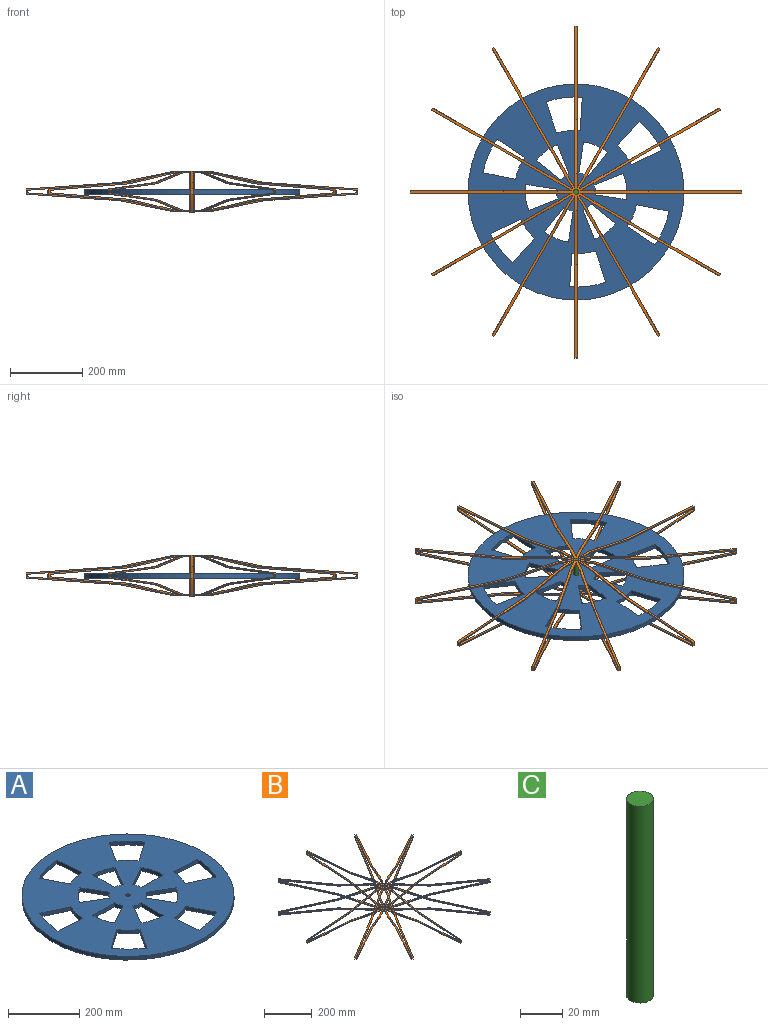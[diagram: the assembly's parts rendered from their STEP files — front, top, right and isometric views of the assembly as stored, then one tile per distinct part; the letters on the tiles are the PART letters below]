
ASSEMBLY  parts=3 mates=2
PART A: 52 faces, bbox 596.9x596.9x12.7 mm
  f0: plane 596.9x596.9mm, normal (0,0,-1), area 207289.9mm2, adj f2,f3,f4,f5,f6,f7,f8,f9
  f1: plane 596.9x596.9mm, normal (0,0,1), area 207289.9mm2, adj f2,f3,f4,f5,f6,f7,f8,f9
  f2: cylinder r=298.45mm len=596.9mm, axis (0,0,-1), area 23815.3mm2, adj f0,f1
  f3: cylinder r=6.35mm len=12.7mm, axis (0,0,-1), area 506.7mm2, adj f0,f1
  f4: plane 75.03x43.12mm, normal (0.5,-0.87,0), area 1099.1mm2, adj f0,f1,f5,f7
  f5: cylinder r=53.62mm len=26.83mm, axis (0,0,1), area 356.5mm2, adj f0,f1,f4,f6
  f6: plane 86.54x12.7mm, normal (0,1,0), area 1099.1mm2, adj f0,f1,f5,f7
  f7: cylinder r=140.16mm len=70.12mm, axis (0,0,1), area 932mm2, adj f0,f1,f4,f6
  f8: cylinder r=140.16mm len=70.04mm, axis (0,0,1), area 932mm2, adj f0,f1,f9,f11
  f9: plane 86.54x12.7mm, normal (1,0,0), area 1099.1mm2, adj f0,f1,f8,f10
  f10: cylinder r=53.62mm len=26.79mm, axis (0,0,1), area 356.5mm2, adj f0,f1,f9,f11
  f11: plane 74.86x43.42mm, normal (-0.87,0.5,0), area 1099.1mm2, adj f0,f1,f8,f10
  f12: plane 75.03x43.12mm, normal (0.87,0.5,0), area 1099.1mm2, adj f0,f1,f13,f15
  f13: cylinder r=140.16mm len=51.41mm, axis (0,0,1), area 932mm2, adj f0,f1,f12,f14
  f14: plane 74.86x43.42mm, normal (-0.5,-0.87,0), area 1099.1mm2, adj f0,f1,f13,f15
  f15: cylinder r=53.62mm len=19.67mm, axis (0,0,1), area 356.5mm2, adj f0,f1,f12,f14
  f16: plane 86.54x12.7mm, normal (-1,0,0), area 1099.1mm2, adj f0,f1,f17,f19
  f17: cylinder r=53.62mm len=26.79mm, axis (0,0,1), area 356.5mm2, adj f0,f1,f16,f18
  f18: plane 74.86x43.42mm, normal (0.87,-0.5,0), area 1099.1mm2, adj f0,f1,f17,f19
  f19: cylinder r=140.16mm len=70.04mm, axis (0,0,1), area 932mm2, adj f0,f1,f16,f18
  f20: cylinder r=140.16mm len=70.12mm, axis (0,0,1), area 932mm2, adj f0,f1,f21,f23
  f21: plane 75.03x43.12mm, normal (-0.5,0.87,0), area 1099.1mm2, adj f0,f1,f20,f22
  f22: cylinder r=53.62mm len=26.83mm, axis (0,0,1), area 356.5mm2, adj f0,f1,f21,f23
  f23: plane 86.54x12.7mm, normal (0,-1,0), area 1099.1mm2, adj f0,f1,f20,f22
  f24: plane 74.86x43.42mm, normal (0.5,0.87,0), area 1099.1mm2, adj f0,f1,f25,f27
  f25: cylinder r=53.62mm len=19.67mm, axis (0,0,1), area 356.5mm2, adj f0,f1,f24,f26
  f26: plane 75.03x43.12mm, normal (-0.87,-0.5,0), area 1099.1mm2, adj f0,f1,f25,f27
  f27: cylinder r=140.16mm len=51.41mm, axis (0,0,1), area 932mm2, adj f0,f1,f24,f26
  f28: plane 82.06x41.29mm, normal (0.89,0.45,0), area 1166.6mm2, adj f0,f1,f29,f31
  f29: cylinder r=171.02mm len=63.19mm, axis (0,0,1), area 838.1mm2, adj f0,f1,f28,f30
  f30: plane 91.54x12.7mm, normal (-1,-0.08,0), area 1166.6mm2, adj f0,f1,f29,f31
  f31: cylinder r=262.88mm len=96.86mm, axis (0,0,1), area 1285.1mm2, adj f0,f1,f28,f30
  f32: cylinder r=171.02mm len=63.19mm, axis (0,0,1), area 838.1mm2, adj f0,f1,f33,f35
  f33: plane 91.54x12.7mm, normal (1,0.08,0), area 1166.6mm2, adj f0,f1,f32,f34
  f34: cylinder r=262.88mm len=96.86mm, axis (0,0,1), area 1285.1mm2, adj f0,f1,f33,f35
  f35: plane 82.06x41.29mm, normal (-0.89,-0.45,0), area 1166.6mm2, adj f0,f1,f32,f34
  f36: cylinder r=171.02mm len=46.8mm, axis (0,0,1), area 838.1mm2, adj f0,f1,f37,f39
  f37: plane 75.47x52.37mm, normal (0.57,-0.82,0), area 1166.6mm2, adj f0,f1,f36,f38
  f38: cylinder r=262.88mm len=71.85mm, axis (0,0,1), area 1285.1mm2, adj f0,f1,f37,f39
  f39: plane 76.79x50.42mm, normal (-0.84,0.55,0), area 1166.6mm2, adj f0,f1,f36,f38
  f40: cylinder r=171.02mm len=63.5mm, axis (0,0,1), area 838.1mm2, adj f0,f1,f41,f43
  f41: plane 83.09x39.18mm, normal (0.43,0.9,0), area 1166.6mm2, adj f0,f1,f40,f42
  f42: cylinder r=262.88mm len=97.41mm, axis (0,0,1), area 1285.1mm2, adj f0,f1,f41,f43
  f43: plane 91.71x12.7mm, normal (-0.06,-1,0), area 1166.6mm2, adj f0,f1,f40,f42
  f44: plane 76.79x50.42mm, normal (0.84,-0.55,0), area 1166.6mm2, adj f0,f1,f45,f47
  f45: cylinder r=171.02mm len=46.8mm, axis (0,0,1), area 838.1mm2, adj f0,f1,f44,f46
  f46: plane 75.47x52.37mm, normal (-0.57,0.82,0), area 1166.6mm2, adj f0,f1,f45,f47
  f47: cylinder r=262.88mm len=71.85mm, axis (0,0,1), area 1285.1mm2, adj f0,f1,f44,f46
  f48: cylinder r=171.02mm len=63.5mm, axis (0,0,1), area 838.1mm2, adj f0,f1,f49,f51
  f49: plane 83.09x39.18mm, normal (-0.43,-0.9,0), area 1166.6mm2, adj f0,f1,f48,f50
  f50: cylinder r=262.88mm len=97.41mm, axis (0,0,1), area 1285.1mm2, adj f0,f1,f49,f51
  f51: plane 91.71x12.7mm, normal (0.06,1,0), area 1166.6mm2, adj f0,f1,f48,f50
PART B: 162 faces, bbox 917.5x917.5x111.6 mm
  f0: plane 387.04x223.46mm, normal (-0.87,-0.5,0), area 3448.3mm2, adj f2,f3,f4,f5,f6,f7,f8,f9
  f1: plane 387.04x223.46mm, normal (0.87,0.5,0), area 3448.3mm2, adj f2,f3,f4,f5,f6,f7,f8,f9
  f2: plane 222.61x132.19mm, normal (0.03,-0.06,-1), area 1612.9mm2, adj f0,f1,f3,f16
  f3: plane 133.6x80.8mm, normal (0.1,-0.17,-0.98), area 976.4mm2, adj f0,f1,f2,f4
  f4: plane 101.94x101.94mm, normal (0,0,-1), area 3305.9mm2, adj f0,f1,f3,f17,f19,f20,f22,f32
  f5: plane 104.62x104.62mm, normal (0,0,1), area 3408mm2, adj f0,f1,f6,f17,f19,f20,f23,f32
  f6: plane 132.44x80.13mm, normal (-0.1,0.17,0.98), area 967.7mm2, adj f0,f1,f5,f7
  f7: plane 225.91x134.1mm, normal (-0.03,0.06,1), area 1637.2mm2, adj f0,f1,f6,f8
  f8: plane 14.41x5.5mm, normal (-0.5,0.87,0), area 91.5mm2, adj f0,f1,f7,f9
  f9: plane 7.4x6.47mm, normal (-0.03,0.06,-1), area 24.3mm2, adj f0,f1,f8,f10
  f10: plane 222.61x132.19mm, normal (-0.04,0.06,-1), area 1612.9mm2, adj f0,f1,f9,f11
  f11: plane 132.58x80.21mm, normal (-0.1,0.17,-0.98), area 968.3mm2, adj f0,f1,f10,f12
  f12: plane 104.31x104.31mm, normal (0,0,-1), area 3396.1mm2, adj f0,f1,f11,f18,f19,f20,f28,f32
  f13: plane 103.54x103.54mm, normal (0,0,1), area 3366.9mm2, adj f0,f1,f14,f18,f19,f20,f29,f32
  f14: plane 132.91x80.4mm, normal (0.1,-0.17,0.98), area 970.8mm2, adj f0,f1,f13,f15
  f15: plane 222.61x132.19mm, normal (0.03,-0.06,1), area 1612.9mm2, adj f0,f1,f14,f16
  f16: plane 7.3x5.5mm, normal (0.5,-0.87,0), area 46.4mm2, adj f0,f1,f2,f15
  f17: cylinder r=6.35mm len=12.7mm, axis (0,0,1), area 141.4mm2, adj f4,f5
  f18: cylinder r=6.35mm len=12.7mm, axis (0,0,1), area 152mm2, adj f12,f13
  f19: plane 387.04x223.46mm, normal (-0.5,-0.87,0), area 3448.3mm2, adj f4,f5,f12,f13,f21,f22,f23,f24
  f20: plane 387.04x223.46mm, normal (0.5,0.87,0), area 3448.3mm2, adj f0,f4,f5,f12,f13,f21,f22,f23
  f21: plane 222.61x132.19mm, normal (0.06,-0.03,-1), area 1612.9mm2, adj f19,f20,f22,f31
  f22: plane 133.6x80.8mm, normal (0.17,-0.1,-0.98), area 976.4mm2, adj f4,f19,f20,f21
  f23: plane 132.44x80.13mm, normal (-0.17,0.1,0.98), area 967.7mm2, adj f5,f19,f20,f24
  f24: plane 225.91x134.1mm, normal (-0.06,0.03,1), area 1637.2mm2, adj f19,f20,f23,f25
  f25: plane 14.41x5.5mm, normal (-0.87,0.5,0), area 91.5mm2, adj f19,f20,f24,f26
  f26: plane 7.4x6.47mm, normal (-0.06,0.03,-1), area 24.3mm2, adj f19,f20,f25,f27
  f27: plane 222.61x132.19mm, normal (-0.06,0.04,-1), area 1612.9mm2, adj f19,f20,f26,f28
  f28: plane 132.58x80.21mm, normal (-0.17,0.1,-0.98), area 968.3mm2, adj f12,f19,f20,f27
  f29: plane 132.91x80.4mm, normal (0.17,-0.1,0.98), area 970.8mm2, adj f13,f19,f20,f30
  f30: plane 222.61x132.19mm, normal (0.06,-0.03,1), area 1612.9mm2, adj f19,f20,f29,f31
  f31: plane 7.3x5.5mm, normal (0.87,-0.5,0), area 46.4mm2, adj f19,f20,f21,f30
  f32: plane 446.92x111.64mm, normal (-1,0,0), area 3448.3mm2, adj f1,f4,f5,f12,f13,f151,f152,f153
  f33: plane 446.92x111.64mm, normal (0,-1,0), area 3448.3mm2, adj f4,f5,f12,f13,f35,f36,f37,f38
  f34: plane 446.92x111.64mm, normal (0,1,0), area 3448.3mm2, adj f4,f5,f12,f13,f19,f35,f36,f37
  f35: plane 253.38x17.72mm, normal (0.07,0,-1), area 1612.9mm2, adj f33,f34,f36,f45
  f36: plane 150.6x31.04mm, normal (0.2,0,-0.98), area 976.4mm2, adj f4,f33,f34,f35
  f37: plane 149.26x30.77mm, normal (-0.2,0,0.98), area 967.7mm2, adj f5,f33,f34,f38
  f38: plane 257.19x17.98mm, normal (-0.07,0,1), area 1637.2mm2, adj f33,f34,f37,f39
  f39: plane 14.41x6.35mm, normal (-1,0,0), area 91.5mm2, adj f33,f34,f38,f40
  f40: plane 6.35x3.81mm, normal (-0.07,0,-1), area 24.3mm2, adj f33,f34,f39,f41
  f41: plane 253.38x17.79mm, normal (-0.07,0,-1), area 1612.9mm2, adj f33,f34,f40,f42
  f42: plane 149.42x30.43mm, normal (-0.2,0,-0.98), area 968.3mm2, adj f12,f33,f34,f41
  f43: plane 149.8x30.51mm, normal (0.2,0,0.98), area 970.8mm2, adj f13,f33,f34,f44
  f44: plane 253.38x17.72mm, normal (0.07,0,1), area 1612.9mm2, adj f33,f34,f43,f45
  f45: plane 7.3x6.35mm, normal (1,0,0), area 46.4mm2, adj f33,f34,f35,f44
  f46: plane 387.04x223.46mm, normal (0.5,-0.87,0), area 3448.3mm2, adj f4,f5,f12,f13,f48,f49,f50,f51
  f47: plane 387.04x223.46mm, normal (-0.5,0.87,0), area 3448.3mm2, adj f4,f5,f12,f13,f33,f48,f49,f50
  f48: plane 222.61x132.19mm, normal (0.06,0.03,-1), area 1612.9mm2, adj f46,f47,f49,f58
  f49: plane 133.6x80.8mm, normal (0.17,0.1,-0.98), area 976.4mm2, adj f4,f46,f47,f48
  f50: plane 132.44x80.13mm, normal (-0.17,-0.1,0.98), area 967.7mm2, adj f5,f46,f47,f51
  f51: plane 225.91x134.1mm, normal (-0.06,-0.03,1), area 1637.2mm2, adj f46,f47,f50,f52
  f52: plane 14.41x5.5mm, normal (-0.87,-0.5,0), area 91.5mm2, adj f46,f47,f51,f53
  f53: plane 7.4x6.47mm, normal (-0.06,-0.03,-1), area 24.3mm2, adj f46,f47,f52,f54
  f54: plane 222.61x132.19mm, normal (-0.06,-0.04,-1), area 1612.9mm2, adj f46,f47,f53,f55
  f55: plane 132.58x80.21mm, normal (-0.17,-0.1,-0.98), area 968.3mm2, adj f12,f46,f47,f54
  f56: plane 132.91x80.4mm, normal (0.17,0.1,0.98), area 970.8mm2, adj f13,f46,f47,f57
  f57: plane 222.61x132.19mm, normal (0.06,0.03,1), area 1612.9mm2, adj f46,f47,f56,f58
  f58: plane 7.3x5.5mm, normal (0.87,0.5,0), area 46.4mm2, adj f46,f47,f48,f57
  f59: plane 387.04x223.46mm, normal (0.87,-0.5,0), area 3448.3mm2, adj f4,f5,f12,f13,f61,f62,f63,f64
  f60: plane 387.04x223.46mm, normal (-0.87,0.5,0), area 3448.3mm2, adj f4,f5,f12,f13,f46,f61,f62,f63
  f61: plane 222.61x132.19mm, normal (0.03,0.06,-1), area 1612.9mm2, adj f59,f60,f62,f71
  f62: plane 133.6x80.8mm, normal (0.1,0.17,-0.98), area 976.4mm2, adj f4,f59,f60,f61
  f63: plane 132.44x80.13mm, normal (-0.1,-0.17,0.98), area 967.7mm2, adj f5,f59,f60,f64
  f64: plane 225.91x134.1mm, normal (-0.03,-0.06,1), area 1637.2mm2, adj f59,f60,f63,f65
  f65: plane 14.41x5.5mm, normal (-0.5,-0.87,0), area 91.5mm2, adj f59,f60,f64,f66
  f66: plane 7.4x6.47mm, normal (-0.03,-0.06,-1), area 24.3mm2, adj f59,f60,f65,f67
  f67: plane 222.61x132.19mm, normal (-0.04,-0.06,-1), area 1612.9mm2, adj f59,f60,f66,f68
  f68: plane 132.58x80.21mm, normal (-0.1,-0.17,-0.98), area 968.3mm2, adj f12,f59,f60,f67
  f69: plane 132.91x80.4mm, normal (0.1,0.17,0.98), area 970.8mm2, adj f13,f59,f60,f70
  f70: plane 222.61x132.19mm, normal (0.03,0.06,1), area 1612.9mm2, adj f59,f60,f69,f71
  f71: plane 7.3x5.5mm, normal (0.5,0.87,0), area 46.4mm2, adj f59,f60,f61,f70
  f72: plane 446.92x111.64mm, normal (1,0,0), area 3448.3mm2, adj f4,f5,f12,f13,f74,f75,f76,f77
  f73: plane 446.92x111.64mm, normal (-1,0,0), area 3448.3mm2, adj f4,f5,f12,f13,f59,f74,f75,f76
  f74: plane 253.38x17.72mm, normal (0,0.07,-1), area 1612.9mm2, adj f72,f73,f75,f84
  f75: plane 150.6x31.04mm, normal (0,0.2,-0.98), area 976.4mm2, adj f4,f72,f73,f74
  f76: plane 149.26x30.77mm, normal (0,-0.2,0.98), area 967.7mm2, adj f5,f72,f73,f77
  f77: plane 257.19x17.98mm, normal (0,-0.07,1), area 1637.2mm2, adj f72,f73,f76,f78
  f78: plane 14.41x6.35mm, normal (0,-1,0), area 91.5mm2, adj f72,f73,f77,f79
  f79: plane 6.35x3.81mm, normal (0,-0.07,-1), area 24.3mm2, adj f72,f73,f78,f80
  f80: plane 253.38x17.79mm, normal (0,-0.07,-1), area 1612.9mm2, adj f72,f73,f79,f81
  f81: plane 149.42x30.43mm, normal (0,-0.2,-0.98), area 968.3mm2, adj f12,f72,f73,f80
  f82: plane 149.8x30.51mm, normal (0,0.2,0.98), area 970.8mm2, adj f13,f72,f73,f83
  f83: plane 253.38x17.72mm, normal (0,0.07,1), area 1612.9mm2, adj f72,f73,f82,f84
  f84: plane 7.3x6.35mm, normal (0,1,0), area 46.4mm2, adj f72,f73,f74,f83
  f85: plane 387.04x223.46mm, normal (0.87,0.5,0), area 3448.3mm2, adj f4,f5,f12,f13,f87,f88,f89,f90
  f86: plane 387.04x223.46mm, normal (-0.87,-0.5,0), area 3448.3mm2, adj f4,f5,f12,f13,f72,f87,f88,f89
  f87: plane 222.61x132.19mm, normal (-0.03,0.06,-1), area 1612.9mm2, adj f85,f86,f88,f97
  f88: plane 133.6x80.8mm, normal (-0.1,0.17,-0.98), area 976.4mm2, adj f4,f85,f86,f87
  f89: plane 132.44x80.13mm, normal (0.1,-0.17,0.98), area 967.7mm2, adj f5,f85,f86,f90
  f90: plane 225.91x134.1mm, normal (0.03,-0.06,1), area 1637.2mm2, adj f85,f86,f89,f91
  f91: plane 14.41x5.5mm, normal (0.5,-0.87,0), area 91.5mm2, adj f85,f86,f90,f92
  f92: plane 7.4x6.47mm, normal (0.03,-0.06,-1), area 24.3mm2, adj f85,f86,f91,f93
  f93: plane 222.61x132.19mm, normal (0.04,-0.06,-1), area 1612.9mm2, adj f85,f86,f92,f94
  f94: plane 132.58x80.21mm, normal (0.1,-0.17,-0.98), area 968.3mm2, adj f12,f85,f86,f93
  f95: plane 132.91x80.4mm, normal (-0.1,0.17,0.98), area 970.8mm2, adj f13,f85,f86,f96
  f96: plane 222.61x132.19mm, normal (-0.03,0.06,1), area 1612.9mm2, adj f85,f86,f95,f97
  f97: plane 7.3x5.5mm, normal (-0.5,0.87,0), area 46.4mm2, adj f85,f86,f87,f96
  f98: plane 387.04x223.46mm, normal (0.5,0.87,0), area 3448.3mm2, adj f4,f5,f12,f13,f100,f101,f102,f103
  f99: plane 387.04x223.46mm, normal (-0.5,-0.87,0), area 3448.3mm2, adj f4,f5,f12,f13,f85,f100,f101,f102
  f100: plane 222.61x132.19mm, normal (-0.06,0.03,-1), area 1612.9mm2, adj f98,f99,f101,f110
  f101: plane 133.6x80.8mm, normal (-0.17,0.1,-0.98), area 976.4mm2, adj f4,f98,f99,f100
  f102: plane 132.44x80.13mm, normal (0.17,-0.1,0.98), area 967.7mm2, adj f5,f98,f99,f103
  f103: plane 225.91x134.1mm, normal (0.06,-0.03,1), area 1637.2mm2, adj f98,f99,f102,f104
  f104: plane 14.41x5.5mm, normal (0.87,-0.5,0), area 91.5mm2, adj f98,f99,f103,f105
  f105: plane 7.4x6.47mm, normal (0.06,-0.03,-1), area 24.3mm2, adj f98,f99,f104,f106
  f106: plane 222.61x132.19mm, normal (0.06,-0.04,-1), area 1612.9mm2, adj f98,f99,f105,f107
  f107: plane 132.58x80.21mm, normal (0.17,-0.1,-0.98), area 968.3mm2, adj f12,f98,f99,f106
  f108: plane 132.91x80.4mm, normal (-0.17,0.1,0.98), area 970.8mm2, adj f13,f98,f99,f109
  f109: plane 222.61x132.19mm, normal (-0.06,0.03,1), area 1612.9mm2, adj f98,f99,f108,f110
  f110: plane 7.3x5.5mm, normal (-0.87,0.5,0), area 46.4mm2, adj f98,f99,f100,f109
  f111: plane 446.92x111.64mm, normal (0,1,0), area 3448.3mm2, adj f4,f5,f12,f13,f113,f114,f115,f116
  f112: plane 446.92x111.64mm, normal (0,-1,0), area 3448.3mm2, adj f4,f5,f12,f13,f98,f113,f114,f115
  f113: plane 253.38x17.72mm, normal (-0.07,0,-1), area 1612.9mm2, adj f111,f112,f114,f123
  f114: plane 150.6x31.04mm, normal (-0.2,0,-0.98), area 976.4mm2, adj f4,f111,f112,f113
  f115: plane 149.26x30.77mm, normal (0.2,0,0.98), area 967.7mm2, adj f5,f111,f112,f116
  f116: plane 257.19x17.98mm, normal (0.07,0,1), area 1637.2mm2, adj f111,f112,f115,f117
  f117: plane 14.41x6.35mm, normal (1,0,0), area 91.5mm2, adj f111,f112,f116,f118
  f118: plane 6.35x3.81mm, normal (0.07,0,-1), area 24.3mm2, adj f111,f112,f117,f119
  f119: plane 253.38x17.79mm, normal (0.07,0,-1), area 1612.9mm2, adj f111,f112,f118,f120
  f120: plane 149.42x30.43mm, normal (0.2,0,-0.98), area 968.3mm2, adj f12,f111,f112,f119
  f121: plane 149.8x30.51mm, normal (-0.2,0,0.98), area 970.8mm2, adj f13,f111,f112,f122
  f122: plane 253.38x17.72mm, normal (-0.07,0,1), area 1612.9mm2, adj f111,f112,f121,f123
  f123: plane 7.3x6.35mm, normal (-1,0,0), area 46.4mm2, adj f111,f112,f113,f122
  f124: plane 387.04x223.46mm, normal (-0.5,0.87,0), area 3448.3mm2, adj f4,f5,f12,f13,f126,f127,f128,f129
  f125: plane 387.04x223.46mm, normal (0.5,-0.87,0), area 3448.3mm2, adj f4,f5,f12,f13,f111,f126,f127,f128
  f126: plane 222.61x132.19mm, normal (-0.06,-0.03,-1), area 1612.9mm2, adj f124,f125,f127,f136
  f127: plane 133.6x80.8mm, normal (-0.17,-0.1,-0.98), area 976.4mm2, adj f4,f124,f125,f126
  f128: plane 132.44x80.13mm, normal (0.17,0.1,0.98), area 967.7mm2, adj f5,f124,f125,f129
  f129: plane 225.91x134.1mm, normal (0.06,0.03,1), area 1637.2mm2, adj f124,f125,f128,f130
  f130: plane 14.41x5.5mm, normal (0.87,0.5,0), area 91.5mm2, adj f124,f125,f129,f131
  f131: plane 7.4x6.47mm, normal (0.06,0.03,-1), area 24.3mm2, adj f124,f125,f130,f132
  f132: plane 222.61x132.19mm, normal (0.06,0.04,-1), area 1612.9mm2, adj f124,f125,f131,f133
  f133: plane 132.58x80.21mm, normal (0.17,0.1,-0.98), area 968.3mm2, adj f12,f124,f125,f132
  f134: plane 132.91x80.4mm, normal (-0.17,-0.1,0.98), area 970.8mm2, adj f13,f124,f125,f135
  f135: plane 222.61x132.19mm, normal (-0.06,-0.03,1), area 1612.9mm2, adj f124,f125,f134,f136
  f136: plane 7.3x5.5mm, normal (-0.87,-0.5,0), area 46.4mm2, adj f124,f125,f126,f135
  f137: plane 387.04x223.46mm, normal (-0.87,0.5,0), area 3448.3mm2, adj f4,f5,f12,f13,f139,f140,f141,f142
  f138: plane 387.04x223.46mm, normal (0.87,-0.5,0), area 3448.3mm2, adj f4,f5,f12,f13,f124,f139,f140,f141
  f139: plane 222.61x132.19mm, normal (-0.03,-0.06,-1), area 1612.9mm2, adj f137,f138,f140,f149
  f140: plane 133.6x80.8mm, normal (-0.1,-0.17,-0.98), area 976.4mm2, adj f4,f137,f138,f139
  f141: plane 132.44x80.13mm, normal (0.1,0.17,0.98), area 967.7mm2, adj f5,f137,f138,f142
  f142: plane 225.91x134.1mm, normal (0.03,0.06,1), area 1637.2mm2, adj f137,f138,f141,f143
  f143: plane 14.41x5.5mm, normal (0.5,0.87,0), area 91.5mm2, adj f137,f138,f142,f144
  f144: plane 7.4x6.47mm, normal (0.03,0.06,-1), area 24.3mm2, adj f137,f138,f143,f145
  f145: plane 222.61x132.19mm, normal (0.04,0.06,-1), area 1612.9mm2, adj f137,f138,f144,f146
  f146: plane 132.58x80.21mm, normal (0.1,0.17,-0.98), area 968.3mm2, adj f12,f137,f138,f145
  f147: plane 132.91x80.4mm, normal (-0.1,-0.17,0.98), area 970.8mm2, adj f13,f137,f138,f148
  f148: plane 222.61x132.19mm, normal (-0.03,-0.06,1), area 1612.9mm2, adj f137,f138,f147,f149
  f149: plane 7.3x5.5mm, normal (-0.5,-0.87,0), area 46.4mm2, adj f137,f138,f139,f148
  f150: plane 446.92x111.64mm, normal (1,0,0), area 3448.3mm2, adj f4,f5,f12,f13,f137,f151,f152,f153
  f151: plane 253.38x17.72mm, normal (0,-0.07,-1), area 1612.9mm2, adj f32,f150,f152,f161
  f152: plane 150.6x31.04mm, normal (0,-0.2,-0.98), area 976.4mm2, adj f4,f32,f150,f151
  f153: plane 149.26x30.77mm, normal (0,0.2,0.98), area 967.7mm2, adj f5,f32,f150,f154
  f154: plane 257.19x17.98mm, normal (0,0.07,1), area 1637.2mm2, adj f32,f150,f153,f155
  f155: plane 14.41x6.35mm, normal (0,1,0), area 91.5mm2, adj f32,f150,f154,f156
  f156: plane 6.35x3.81mm, normal (0,0.07,-1), area 24.3mm2, adj f32,f150,f155,f157
  f157: plane 253.38x17.79mm, normal (0,0.07,-1), area 1612.9mm2, adj f32,f150,f156,f158
  f158: plane 149.42x30.43mm, normal (0,0.2,-0.98), area 968.3mm2, adj f12,f32,f150,f157
  f159: plane 149.8x30.51mm, normal (0,-0.2,0.98), area 970.8mm2, adj f13,f32,f150,f160
  f160: plane 253.38x17.72mm, normal (0,-0.07,1), area 1612.9mm2, adj f32,f150,f159,f161
  f161: plane 7.3x6.35mm, normal (0,-1,0), area 46.4mm2, adj f32,f150,f151,f160
PART C: 3 faces, bbox 12.7x12.7x114.3 mm
  f0: cylinder r=6.35mm len=114.3mm, axis (0,0,-1), area 4560.4mm2, adj f1,f2
  f1: plane 12.7x12.7mm, normal (0,0,1), area 126.7mm2, adj f0
  f2: plane 12.7x12.7mm, normal (0,0,-1), area 126.7mm2, adj f0
PLACE A rot(axis=(0,0,-1),8.4deg) t=(-3.97,-1.91,-0.88)mm
PLACE B t=(-3.97,-1.91,0.58)mm fixed
PLACE C rot(axis=(0,0,-1),8.4deg) t=(-3.97,-1.91,-0.88)mm
MATE revolute C.f0 <-> B.f17  axis (0,0,-1) through (-3.97,-1.91,56.27)mm
MATE fastened C.f0 <-> A.f2  axis (0,0,-1) through (-3.97,-1.91,-0.88)mm
